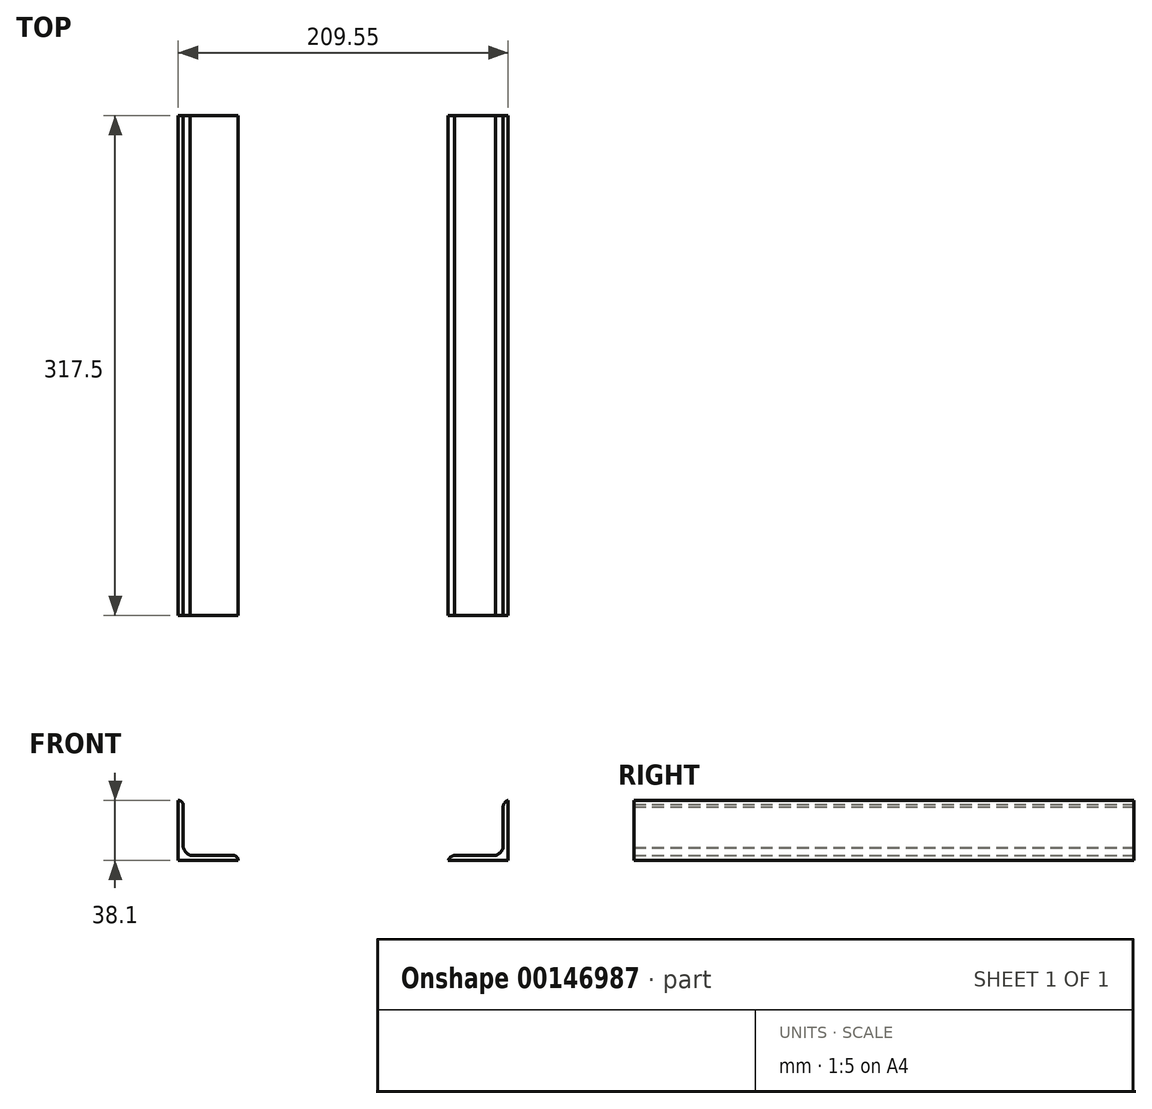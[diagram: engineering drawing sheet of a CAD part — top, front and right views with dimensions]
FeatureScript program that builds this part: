
annotation { "Feature Type Name" : "Feature", "Feature Type Description" : "" }
export const myFeature = defineFeature(function(context is Context, id is Id, definition is map)
    precondition{}
    {
        {
            var Q0;
            Q0=qCreatedBy(makeId("Front.planeOp"),FACE);
            var sketch = newSketch(context, id + "F0", { "sketchPlane" : qUnion([Q0])});
            skLineSegment(sketch, "E0.bottom", {"start": v(-41.27, 0) * mm, "end": v(-38.1, 0) * mm});
            skLineSegment(sketch, "E0.left", {"start": v(-41.27, 0) * mm, "end": v(-41.28, 38.1) * mm});
            skLineSegment(sketch, "E0.right", {"start": v(-38.1, 8.37) * mm, "end": v(-38.1, 35.52) * mm});
            skLineSegment(sketch, "E1.bottom", {"start": v(-41.27, 0) * mm, "end": v(-3.18, 0) * mm});
            skLineSegment(sketch, "E1.top", {"start": v(-33.6, 3.17) * mm, "end": v(-6.35, 3.17) * mm});
            skLineSegment(sketch, "E1.left", {"start": v(-41.27, 0) * mm, "end": v(-41.27, 3.17) * mm});
            skLineSegment(sketch, "E2.bottom", {"start": v(165.1, 0) * mm, "end": v(168.27, 0) * mm});
            skLineSegment(sketch, "E2.left", {"start": v(165.1, 7.96) * mm, "end": v(165.1, 34.08) * mm});
            skLineSegment(sketch, "E2.right", {"start": v(168.27, 0) * mm, "end": v(168.27, 38.1) * mm});
            skLineSegment(sketch, "E3.bottom", {"start": v(168.27, 0) * mm, "end": v(130.17, 0) * mm});
            skLineSegment(sketch, "E3.top", {"start": v(160.2, 3.18) * mm, "end": v(134.08, 3.18) * mm});
            skLineSegment(sketch, "E3.left", {"start": v(168.27, 0) * mm, "end": v(168.27, 3.18) * mm});
            skArc(sketch, "E4", {"start": v(-38.1, 35.52) * mm, "mid": v(-39.23, 37.37) * mm, "end": v(-41.28, 38.1) * mm});
            skArc(sketch, "E5", {"start": v(-3.18, 0) * mm, "mid": v(-4.1, 2.24) * mm, "end": v(-6.35, 3.17) * mm});
            skPoint(sketch, "E6.orphan", {"position": v(-38.1, 38.1) * mm});
            skArc(sketch, "E7", {"start": v(134.08, 3.18) * mm, "mid": v(131.74, 2.06) * mm, "end": v(130.17, 0) * mm});
            skArc(sketch, "E8", {"start": v(168.27, 38.1) * mm, "mid": v(166.08, 36.57) * mm, "end": v(165.1, 34.08) * mm});
            skPoint(sketch, "E9.orphan", {"position": v(165.1, 38.1) * mm});
            skArc(sketch, "E10", {"start": v(160.2, 3.18) * mm, "mid": v(163.3, 4.9) * mm, "end": v(165.1, 7.96) * mm});
            skArc(sketch, "E11", {"start": v(-38.1, 8.37) * mm, "mid": v(-36.47, 5.24) * mm, "end": v(-33.6, 3.17) * mm});
            skLineSegment(sketch, "E12", {"start": v(-3.17, 0) * mm, "end": v(130.17, 0) * mm});
            skSolve(sketch);
        }
        {
            var Q0;
            Q0 = qSketchRegion(id + "F0", true);
            extrude(context, id + "F1", {"entities" : qUnion([Q0]), "depth" : 317.5 * mm});
        }
    });
